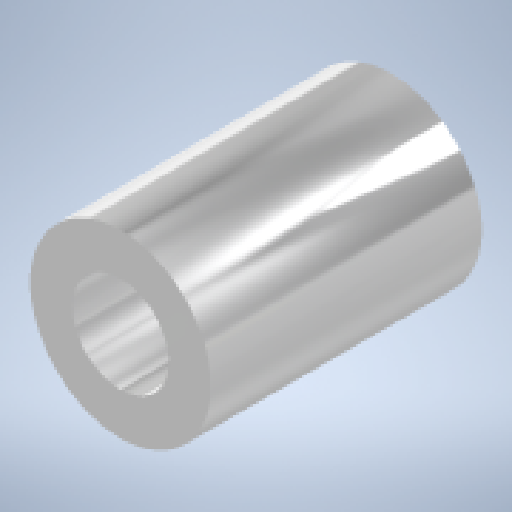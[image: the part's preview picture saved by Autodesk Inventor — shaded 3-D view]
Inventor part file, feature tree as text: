
AUTODESK INVENTOR PART (.ipt)
format: ipt  version: 2024 (Build 280153000, 153)  size: 140,800 bytes
history: native  units: mm
features: other x1, extrude x1, sketch x1
ambient origin geometry x8: Origin, YZ Plane, XZ Plane, XY Plane, X Axis, Y Axis, Z Axis, Center Point
bodies: Body1 (feature_tree)
feature tree (3):
  other  "ソリッド1"
  extrude  "押し出し1"  Depth=3.2mm
  sketch  "スケッチ1"
